# Revit family: Plymold-Essentials-Spectrum-
name_source: partatom
category: Furniture
units: mm (PartAtom-declared; Revit-internal decimal feet)

## family parameters
Always vertical = Yes
Cut with Voids When Loaded = No
OmniClass Number = 23.40.20.00
OmniClass Title = General Furniture and Specialties
Render Appearance Source = Family Geometry
Room Calculation Point = No
Shared = No
Work Plane-Based = No

## types (2) — shared parameters
Assembly Code = E2020200
Brand = Spectrum & Harmony
Default Elevation = 0"
FRAME MATERIAL = PLY - Starburst Silver Powdercoat
GLIDES MATERIAL = PLY - Plastic Black
Keynote = 12500
Manufacturer = Plymold
Product Documentation Link = https://plymold.com
Revit Model Built By = https://www.servex-us.com
SEAT MATERIAL = PLY - Vinyl - Leap Frog
Sustainability = https://plymold.com
Type Comments = Chairs & Barstools
URL = https://plymold.com
Width = 16"
zero-valued in all types: Cost

## per-type parameters (varying)
| type | Depth | Description | Height |
| 6111PS | 20" | Spectrum Chair- 16”W x 20”D x 35”H | 35" |
| 6113PS | 22 1/2" | Spectrum Barstool - 16”W x 22 1/2"D x 46 1/2"H | 46 1/2" |

note: column(s) folded — value = type name in every type: Model

## geometry (parser evidence)
native form markers: Sweep x3
no freeform markers — native parametric forms only
